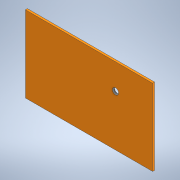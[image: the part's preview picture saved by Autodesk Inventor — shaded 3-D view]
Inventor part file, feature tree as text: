
AUTODESK INVENTOR PART (.ipt)
format: ipt  version: 2021 (Build 250183000, 183)  size: 114,688 bytes
history: native  units: in
note: dims shown in document units (in); Inventor stores cm internally (conversion verified against a paired STEP export)
features: extrude x2, sketch x2, pattern_linear x1, projected_geometry x1
ambient origin geometry x8: Origin, YZ Plane, XZ Plane, XY Plane, X Axis, Y Axis, Z Axis, Center Point
bodies: Solid1 (feature_tree)
feature tree (6):
  extrude  "Extrusion1"  Depth=0.004in TaperAngle=0.0deg
  extrude  "Extrusion2"  Depth=0.0728in
  pattern_linear  "Rectangular Pattern1"  Spacing1=0.0in  [1 undecoded]
  sketch  "Sketch1"  dims[d0=0.25in d2=0.004in d3=0.0in]
  sketch  "Sketch2"  dims[d4=0.012in d5=0.0728in d6=0.0in d7=0.0in d8=1.1811in d10=0.05in d12=0.1in d14=0.05in]
  projected_geometry  "Projected Loop1"
note: 1 required parameter value undecoded (feature->parameter linkage not recoverable at this tier; creation-order binding heuristic only, values carry confidence <= 0.55)
